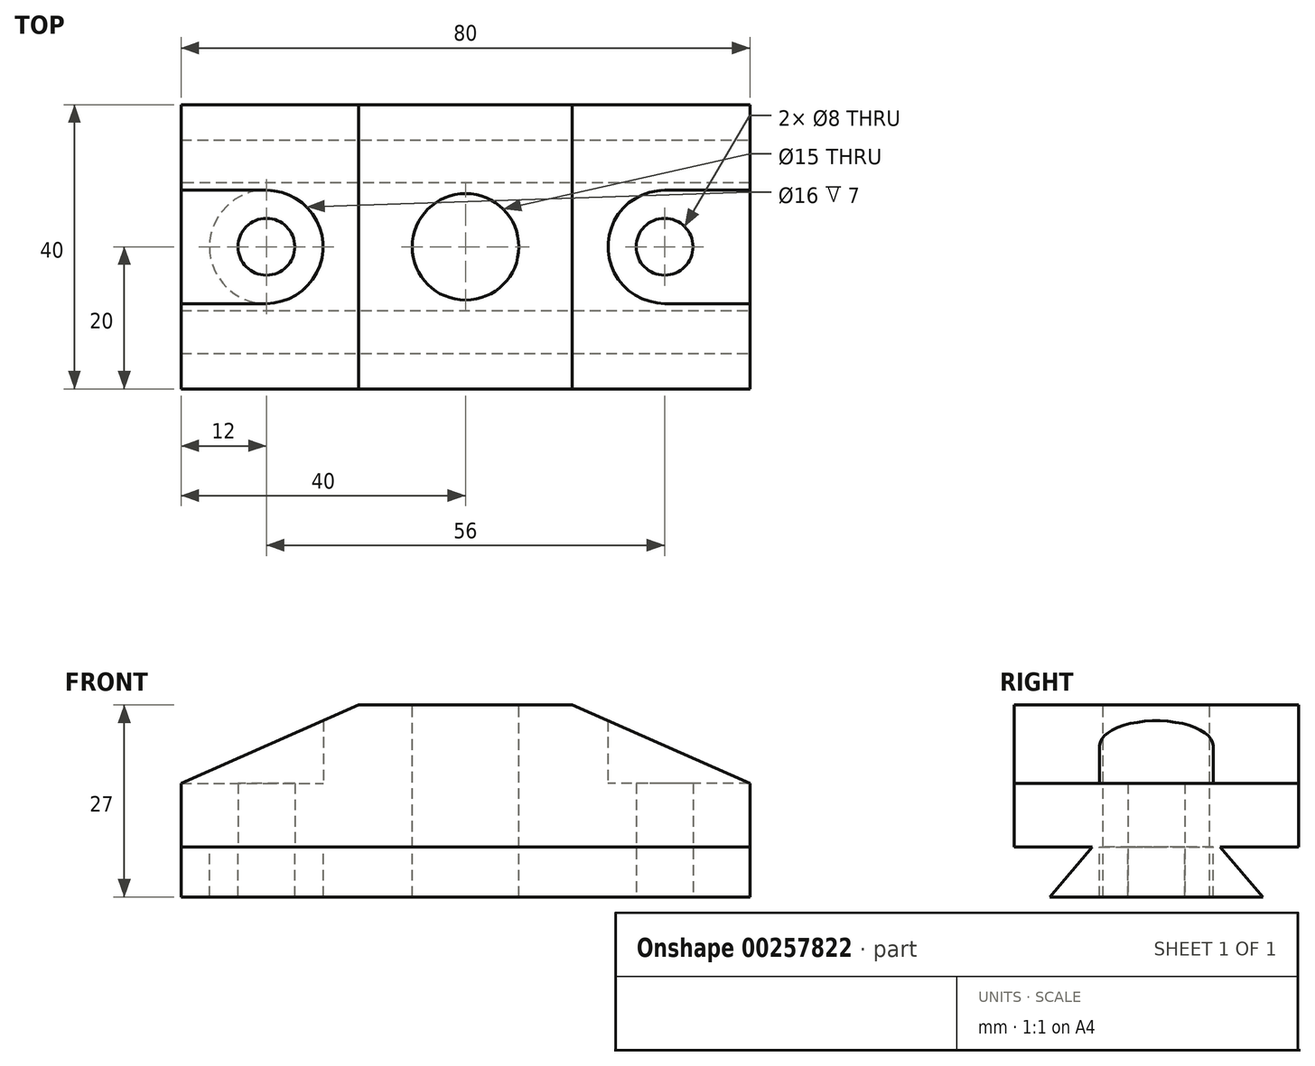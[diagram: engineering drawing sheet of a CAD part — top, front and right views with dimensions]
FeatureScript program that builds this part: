
annotation { "Feature Type Name" : "Feature", "Feature Type Description" : "" }
export const myFeature = defineFeature(function(context is Context, id is Id, definition is map)
    precondition{}
    {
        {
            var Q0;
            Q0=qCreatedBy(makeId("Top.planeOp"),FACE);
            var sketch = newSketch(context, id + "F0", { "sketchPlane" : qUnion([Q0])});
            skLineSegment(sketch, "E0.bottom", {"start": v(-40, 30) * mm, "end": v(40, 30) * mm});
            skLineSegment(sketch, "E0.top", {"start": v(-40, 0) * mm, "end": v(40, 0) * mm});
            skLineSegment(sketch, "E0.left", {"start": v(-40, 30) * mm, "end": v(-40, 0) * mm});
            skLineSegment(sketch, "E0.right", {"start": v(40, 30) * mm, "end": v(40, 0) * mm});
            skSolve(sketch);
        }
        {
            var Q0;
            Q0=makeQuery(id+"F0.imprint","IMPRINT",FACE,{"disambiguationData":[TD([[makeQuery(id+"F0.imprint","IMPRINT",EDGE,{"derivedFrom":sQuery(id+"F0.wireOp",EDGE,"E0.bottom")}),-1.0]])]});
            extrude(context, id + "F1", {"entities" : qUnion([Q0]), "depth" : 7 * mm});
        }
        {
            var Q0;
            Q0=makeQuery(id+"F1.opExtrude","CAP_EDGE",EDGE,{"disambiguationData":[OSD([sQuery(id+"F0.wireOp",EDGE,"E0.top")])],"isStart":false});
            chamfer(context, id + "F2", {"entities" : qUnion([Q0]), "chamferType" : ChamferType.TWO_OFFSETS, "width1" : 6 * mm, "oppositeDirection" : false, "width2" : 7 * mm, "tangentPropagation" : true});
        }
        {
            var Q0;
            Q0=makeQuery(id+"F1.opExtrude","CAP_EDGE",EDGE,{"disambiguationData":[OSD([sQuery(id+"F0.wireOp",EDGE,"E0.bottom")])],"isStart":false});
            chamfer(context, id + "F3", {"entities" : qUnion([Q0]), "chamferType" : ChamferType.TWO_OFFSETS, "width1" : 7 * mm, "oppositeDirection" : false, "width2" : 6 * mm, "tangentPropagation" : true});
        }
        {
            var Q0;
            Q0=makeQuery(id+"F1.opExtrude","CAP_FACE",FACE,{"disambiguationData":[OSD([sQuery(id+"F0.wireOp",EDGE,"E0.bottom"),sQuery(id+"F0.wireOp",EDGE,"E0.top"),sQuery(id+"F0.wireOp",EDGE,"E0.left"),sQuery(id+"F0.wireOp",EDGE,"E0.right")])],"isStart":false});
            var sketch = newSketch(context, id + "F4", { "sketchPlane" : qUnion([Q0])});
            skLineSegment(sketch, "E1.bottom", {"start": v(-40, -5) * mm, "end": v(40, -5) * mm});
            skLineSegment(sketch, "E1.top", {"start": v(-40, 35) * mm, "end": v(40, 35) * mm});
            skLineSegment(sketch, "E1.left", {"start": v(-40, -5) * mm, "end": v(-40, 35) * mm});
            skLineSegment(sketch, "E1.right", {"start": v(40, -5) * mm, "end": v(40, 35) * mm});
            skLineSegment(sketch, "E2.bottom", {"start": v(-40, 23) * mm, "end": v(-28, 23) * mm});
            skLineSegment(sketch, "E2.top", {"start": v(-40, 7) * mm, "end": v(-28, 7) * mm});
            skLineSegment(sketch, "E2.left", {"start": v(-40, 23) * mm, "end": v(-40, 7) * mm});
            skLineSegment(sketch, "E2.right", {"start": v(-28, 23) * mm, "end": v(-28, 7) * mm});
            skCircle(sketch, "E3", {"center": v(-28, 15) * mm, "radius": 8 * mm});
            skLineSegment(sketch, "E4.bottom", {"start": v(40, 7) * mm, "end": v(28, 7) * mm});
            skLineSegment(sketch, "E4.top", {"start": v(40, 23) * mm, "end": v(28, 23) * mm});
            skLineSegment(sketch, "E4.left", {"start": v(40, 7) * mm, "end": v(40, 23) * mm});
            skCircle(sketch, "E5", {"center": v(28, 15) * mm, "radius": 8 * mm});
            skCircle(sketch, "E6", {"center": v(-28, 15) * mm, "radius": 4 * mm});
            skCircle(sketch, "E7", {"center": v(28, 15) * mm, "radius": 4 * mm});
            skSolve(sketch);
        }
        {
            var Q0;
            {var subQ3=sQuery(id+"F4.wireOp",EDGE,"E2.bottom");Q0=makeQuery(id+"F4.imprint","IMPRINT",FACE,{"disambiguationData":[TD([[makeQuery(id+"F4.imprint","IMPRINT",EDGE,{"derivedFrom":subQ3}),1.0]])]});}
            var Q1;
            {var subQ0=sQuery(id+"F4.wireOp",EDGE,"E1.bottom");Q1=makeQuery(id+"F4.imprint","IMPRINT",FACE,{"disambiguationData":[TD([[makeQuery(id+"F4.imprint","IMPRINT",EDGE,{"derivedFrom":subQ0}),1.0]])]});}
            var Q2;
            {var subQ0=sQuery(id+"F4.wireOp",EDGE,"E1.top");Q2=makeQuery(id+"F4.imprint","IMPRINT",FACE,{"disambiguationData":[TD([[makeQuery(id+"F4.imprint","IMPRINT",EDGE,{"derivedFrom":subQ0}),-1.0]])]});}
            extrude(context, id + "F5", {"entities" : qUnion([Q0, Q1, Q2]), "operationType" : NewBodyOperationType.ADD, "depth" : 20 * mm});
        }
        {
            var Q0;
            Q0=makeQuery(id+"F5.opExtrude","CAP_EDGE",EDGE,{"disambiguationData":[OSD([sQuery(id+"F4.wireOp",EDGE,"E1.left")])],"isStart":false});
            chamfer(context, id + "F6", {"entities" : qUnion([Q0]), "chamferType" : ChamferType.TWO_OFFSETS, "width1" : 25 * mm, "oppositeDirection" : false, "width2" : 11 * mm, "tangentPropagation" : true});
        }
        {
            var Q0;
            Q0=makeQuery(id+"F5.opExtrude","CAP_EDGE",EDGE,{"disambiguationData":[OSD([sQuery(id+"F4.wireOp",EDGE,"E1.right")])],"isStart":false});
            chamfer(context, id + "F7", {"entities" : qUnion([Q0]), "chamferType" : ChamferType.TWO_OFFSETS, "width1" : 11 * mm, "oppositeDirection" : false, "width2" : 25 * mm, "tangentPropagation" : true});
        }
        {
            var Q0;
            Q0=makeQuery(id+"F5.opExtrude","CAP_FACE",FACE,{"disambiguationData":[OSD([sQuery(id+"F4.wireOp",EDGE,"E1.bottom"),sQuery(id+"F4.wireOp",EDGE,"E1.top"),sQuery(id+"F4.wireOp",EDGE,"E1.left"),sQuery(id+"F4.wireOp",EDGE,"E1.right")])],"isStart":false});
            var sketch = newSketch(context, id + "F8", { "sketchPlane" : qUnion([Q0])});
            skCircle(sketch, "E8", {"center": v(0, 15) * mm, "radius": 7.5 * mm});
            skPoint(sketch, "E8.centerSnap0", {"position": v(0, -5) * mm});
            skSolve(sketch);
        }
        {
            var Q0;
            Q0=makeQuery(id+"F8.imprint","IMPRINT",FACE,{"disambiguationData":[TD([[makeQuery(id+"F8.imprint","IMPRINT",EDGE,{"derivedFrom":sQuery(id+"F8.wireOp",EDGE,"E8")}),1.0]])]});
            extrude(context, id + "F9", {"entities" : qUnion([Q0]), "operationType" : NewBodyOperationType.REMOVE, "endBound" : BoundingType.UP_TO_NEXT, "oppositeDirection" : true, "depth" : 50 * mm});
        }
        {
            var Q0;
            {var subQ0=sQuery(id+"F4.wireOp",EDGE,"E2.right");Q0=makeQuery(id+"F4.imprint","IMPRINT",FACE,{"disambiguationData":[TD([[makeQuery(id+"F4.imprint","IMPRINT",EDGE,{"derivedFrom":subQ0}),1.0]])]});}
            var Q1;
            {var subQ0=sQuery(id+"F4.wireOp",EDGE,"E2.right");Q1=makeQuery(id+"F4.imprint","IMPRINT",FACE,{"disambiguationData":[TD([[makeQuery(id+"F4.imprint","IMPRINT",EDGE,{"derivedFrom":subQ0}),-1.0]])]});}
            var Q2;
            {var subQ0=sQuery(id+"F4.wireOp",EDGE,"E2.bottom");Q2=makeQuery(id+"F4.imprint","IMPRINT",FACE,{"disambiguationData":[TD([[makeQuery(id+"F4.imprint","IMPRINT",EDGE,{"derivedFrom":subQ0}),-1.0]])]});}
            var Q3;
            {var subQ0=sQuery(id+"F4.wireOp",EDGE,"E5");var subQ1=makeQuery(id+"F4.imprint","INTERSECT",VERTEX,{"derivedFrom":[sQuery(id+"F4.wireOp",EDGE,"E4.bottom"),subQ0]});Q3=makeQuery(id+"F4.imprint","IMPRINT",FACE,{"disambiguationData":[TD([[makeQuery(id+"F4.imprint","IMPRINT",EDGE,{"disambiguationData":[TD([[subQ1,-1.0]])],"derivedFrom":subQ0}),1.0]])]});}
            var Q4;
            {var subQ0=sQuery(id+"F4.wireOp",EDGE,"E4.bottom");Q4=makeQuery(id+"F4.imprint","IMPRINT",FACE,{"disambiguationData":[TD([[makeQuery(id+"F4.imprint","IMPRINT",EDGE,{"derivedFrom":subQ0}),-1.0]])]});}
            extrude(context, id + "F10", {"entities" : qUnion([Q0, Q1, Q2, Q3, Q4]), "operationType" : NewBodyOperationType.ADD, "depth" : (20 - 11) * mm});
        }
        {
            var Q0;
            {var subQ0=sQuery(id+"F4.wireOp",EDGE,"E6");var subQ1=sQuery(id+"F4.wireOp",EDGE,"E2.right");var subQ2=makeQuery(id+"F4.imprint","INTERSECT",VERTEX,{"disambiguationData":[OD(0.0)],"derivedFrom":[subQ1,subQ0]});Q0=makeQuery(id+"F4.imprint","IMPRINT",FACE,{"disambiguationData":[TD([[makeQuery(id+"F4.imprint","IMPRINT",EDGE,{"disambiguationData":[TD([[subQ2,-1.0]])],"derivedFrom":subQ1}),1.0]])]});}
            var Q1;
            {var subQ0=sQuery(id+"F4.wireOp",EDGE,"E6");var subQ1=sQuery(id+"F4.wireOp",EDGE,"E2.right");var subQ2=makeQuery(id+"F4.imprint","INTERSECT",VERTEX,{"disambiguationData":[OD(0.0)],"derivedFrom":[subQ1,subQ0]});Q1=makeQuery(id+"F4.imprint","IMPRINT",FACE,{"disambiguationData":[TD([[makeQuery(id+"F4.imprint","IMPRINT",EDGE,{"disambiguationData":[TD([[subQ2,-1.0]])],"derivedFrom":subQ1}),-1.0]])]});}
            var Q2;
            Q2=makeQuery(id+"F4.imprint","IMPRINT",FACE,{"disambiguationData":[TD([[makeQuery(id+"F4.imprint","IMPRINT",EDGE,{"derivedFrom":sQuery(id+"F4.wireOp",EDGE,"E7")}),1.0]])]});
            extrude(context, id + "F11", {"entities" : qUnion([Q0, Q1, Q2]), "operationType" : NewBodyOperationType.REMOVE, "oppositeDirection" : true, "depth" : 25 * mm});
        }
    });
